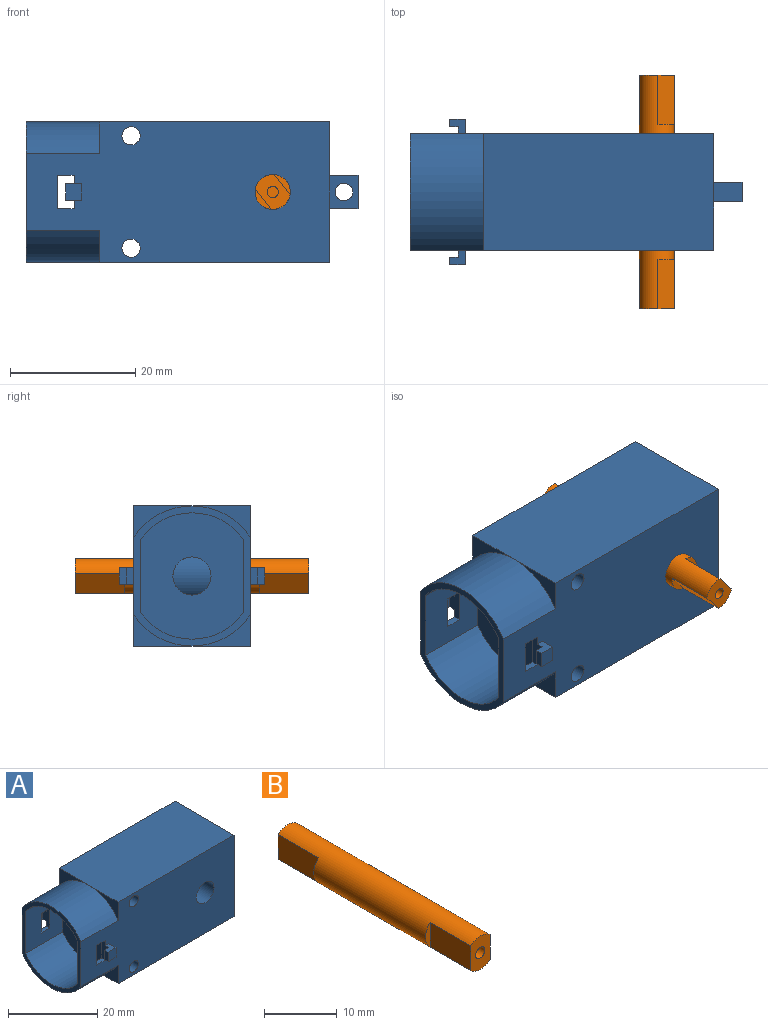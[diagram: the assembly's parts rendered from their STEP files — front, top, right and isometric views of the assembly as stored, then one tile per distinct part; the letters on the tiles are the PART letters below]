
ASSEMBLY  parts=2 mates=1
PART A: 63 faces, bbox 53.1x23.3x22.4 mm
  f0: plane 48.6x22.4mm, normal (0,-1,0), area 914.4mm2, adj f20,f21,f22,f23,f25,f26,f27,f28
  f1: plane 48.6x22.4mm, normal (0,1,0), area 914.4mm2, adj f19,f22,f23,f24,f25,f26,f27,f28
  f2: plane 15.7x0.64mm, normal (0,0,-1), area 10mm2, adj f6,f7,f11,f12
  f3: plane 15.7x0.64mm, normal (0,0,1), area 10mm2, adj f6,f10,f11,f12
  f4: plane 19.4x15.7mm, normal (-1,0,0), area 304.3mm2, adj f5,f9,f11,f12,f13,f14,f16,f17
  f5: plane 27.44x15.7mm, normal (0,0,-1), area 430.8mm2, adj f4,f7,f11,f12
  f6: plane 19.4x15.7mm, normal (1,0,0), area 275.4mm2, adj f2,f3,f11,f12,f18
  f7: cylinder r=2.95mm len=15.7mm, axis (0,1,0), area 168.3mm2, adj f2,f5,f11,f12
  f8: cylinder r=4.3mm len=15.7mm, axis (0,1,0), area 424.2mm2, adj f11,f12
  f9: plane 27.44x15.7mm, normal (0,0,1), area 430.8mm2, adj f4,f10,f11,f12
  f10: cylinder r=2.95mm len=15.7mm, axis (0,1,0), area 168.3mm2, adj f3,f9,f11,f12
  f11: plane 33.8x19.4mm, normal (0,1,0), area 561.9mm2, adj f2,f3,f4,f5,f6,f7,f8,f9
  f12: plane 33.8x19.4mm, normal (0,-1,0), area 561.9mm2, adj f2,f3,f4,f5,f6,f7,f8,f9
  f13: plane 1.11x0.1mm, normal (0,0,1), area 0.1mm2, adj f4,f15,f16,f17
  f14: plane 1.11x0.1mm, normal (0,0,-1), area 0.1mm2, adj f4,f15,f16,f17
  f15: cylinder r=2.9mm len=2.4mm, axis (0,1,0), area 0.2mm2, adj f13,f14,f16,f17
  f16: plane 2.4x1.11mm, normal (0,1,0), area 2.2mm2, adj f4,f13,f14,f15
  f17: plane 2.4x1.11mm, normal (0,-1,0), area 2.2mm2, adj f4,f13,f14,f15
  f18: cylinder r=3.05mm len=6.1mm, axis (-1,0,0), area 28.7mm2, adj f6,f42
  f19: plane 9.35x5.03mm, normal (-1,0,0), area 13.9mm2, adj f1,f27,f36
  f20: plane 9.35x5.03mm, normal (-1,0,0), area 13.9mm2, adj f0,f27,f36
  f21: plane 9.35x5.03mm, normal (-1,0,0), area 13.9mm2, adj f0,f23,f35
  f22: plane 22.4x18.7mm, normal (1,0,0), area 402.1mm2, adj f0,f1,f23,f27,f29,f31,f33,f34
  f23: plane 36.8x18.7mm, normal (0,0,1), area 688.2mm2, adj f0,f1,f21,f22,f24
  f24: plane 9.35x5.03mm, normal (-1,0,0), area 13.9mm2, adj f1,f23,f35
  f25: cylinder r=1.45mm len=18.7mm, axis (0,1,0), area 170.4mm2, adj f0,f1
  f26: cylinder r=2.8mm len=18.7mm, axis (0,1,0), area 329mm2, adj f0,f1
  f27: plane 36.8x18.7mm, normal (0,0,-1), area 688.2mm2, adj f0,f1,f19,f20,f22
  f28: cylinder r=1.45mm len=18.7mm, axis (0,1,0), area 170.4mm2, adj f0,f1
  f29: plane 4.5x3.1mm, normal (0,0,-1), area 13.9mm2, adj f22,f30,f33,f34
  f30: plane 5.4x3.1mm, normal (1,0,0), area 16.7mm2, adj f29,f31,f33,f34
  f31: plane 4.5x3.1mm, normal (0,0,1), area 13.9mm2, adj f22,f30,f33,f34
  f32: cylinder r=1.4mm len=3.1mm, axis (0,1,0), area 27.3mm2, adj f33,f34
  f33: plane 5.4x4.5mm, normal (0,-1,0), area 18.1mm2, adj f22,f29,f30,f31,f32
  f34: plane 5.4x4.5mm, normal (0,1,0), area 18.1mm2, adj f22,f29,f30,f31,f32
  f35: cylinder r=11.2mm len=18.7mm, axis (1,0,0), area 261.1mm2, adj f0,f1,f21,f24,f37
  f36: cylinder r=11.2mm len=18.7mm, axis (1,0,0), area 261.1mm2, adj f0,f1,f19,f20,f37
  f37: plane 22.4x18.7mm, normal (-1,0,0), area 72mm2, adj f0,f1,f35,f36,f38,f39,f40,f41
  f38: cylinder r=10.1mm len=16.5mm, axis (-1,0,0), area 227.8mm2, adj f37,f39,f41,f42
  f39: plane 11.8x11.65mm, normal (0,-1,0), area 122.9mm2, adj f37,f38,f40,f42,f47,f48,f49,f50
  f40: cylinder r=10.1mm len=16.5mm, axis (-1,0,0), area 227.8mm2, adj f37,f39,f41,f42
  f41: plane 11.8x11.65mm, normal (0,1,0), area 122.9mm2, adj f37,f38,f40,f42,f43,f44,f45,f46
  f42: plane 20.2x16.5mm, normal (-1,0,0), area 261.9mm2, adj f18,f38,f39,f40,f41
  f43: plane 2.7x1.1mm, normal (0,0,-1), area 3mm2, adj f0,f41,f44,f46
  f44: plane 5.4x2.2mm, normal (-1,0,0), area 8.8mm2, adj f0,f41,f43,f45,f60,f61,f62
  f45: plane 2.7x1.1mm, normal (0,0,1), area 3mm2, adj f0,f41,f44,f46
  f46: plane 5.4x1.1mm, normal (1,0,0), area 5.9mm2, adj f0,f41,f43,f45
  f47: plane 5.4x1.1mm, normal (1,0,0), area 5.9mm2, adj f1,f39,f48,f50
  f48: plane 2.7x1.1mm, normal (0,0,1), area 3mm2, adj f1,f39,f47,f49
  f49: plane 5.4x2.2mm, normal (-1,0,0), area 8.8mm2, adj f1,f39,f48,f50,f54,f55,f56
  f50: plane 2.7x1.1mm, normal (0,0,-1), area 3mm2, adj f1,f39,f47,f49
  f51: plane 2.6x2.3mm, normal (1,0,0), area 6mm2, adj f1,f52,f55,f56
  f52: plane 2.6x2.5mm, normal (0,1,0), area 6.5mm2, adj f51,f53,f55,f56
  f53: plane 2.6x1.2mm, normal (-1,0,0), area 3.1mm2, adj f52,f54,f55,f56
  f54: plane 2.6x1.35mm, normal (0,-1,0), area 3.5mm2, adj f49,f53,f55,f56
  f55: plane 2.5x2.3mm, normal (0,0,1), area 4.3mm2, adj f1,f49,f51,f52,f53,f54
  f56: plane 2.5x2.3mm, normal (0,0,-1), area 4.3mm2, adj f1,f49,f51,f52,f53,f54
  f57: plane 2.6x2.3mm, normal (1,0,0), area 6mm2, adj f0,f58,f61,f62
  f58: plane 2.6x2.5mm, normal (0,-1,0), area 6.5mm2, adj f57,f59,f61,f62
  f59: plane 2.6x1.2mm, normal (-1,0,0), area 3.1mm2, adj f58,f60,f61,f62
  f60: plane 2.6x1.35mm, normal (0,1,0), area 3.5mm2, adj f44,f59,f61,f62
  f61: plane 2.5x2.3mm, normal (0,0,1), area 4.3mm2, adj f0,f44,f57,f58,f59,f60
  f62: plane 2.5x2.3mm, normal (0,0,-1), area 4.3mm2, adj f0,f44,f57,f58,f59,f60
PART B: 15 faces, bbox 5.6x37.4x5.6 mm
  f0: cylinder r=2.8mm len=37.4mm, axis (0,-1,0), area 511.2mm2, adj f1,f2,f3,f4,f5,f8,f9,f10
  f1: plane 5.6x3.76mm, normal (0,1,0), area 16.8mm2, adj f0,f2,f4,f6
  f2: plane 7.85x4.15mm, normal (1,0,0), area 32.6mm2, adj f0,f1,f3
  f3: plane 4.15x0.92mm, normal (0,1,0), area 2.6mm2, adj f0,f2
  f4: plane 7.85x4.15mm, normal (-1,0,0), area 32.6mm2, adj f0,f1,f5
  f5: plane 4.15x0.92mm, normal (0,1,0), area 2.6mm2, adj f0,f4
  f6: cylinder r=0.9mm len=7.85mm, axis (0,1,0), area 44.4mm2, adj f1,f7
  f7: plane 1.8x1.8mm, normal (0,1,0), area 2.5mm2, adj f6
  f8: plane 5.6x3.76mm, normal (0,-1,0), area 16.8mm2, adj f0,f9,f11,f13
  f9: plane 7.85x4.15mm, normal (1,0,0), area 32.6mm2, adj f0,f8,f10
  f10: plane 4.15x0.92mm, normal (0,-1,0), area 2.6mm2, adj f0,f9
  f11: plane 7.85x4.15mm, normal (-1,0,0), area 32.6mm2, adj f0,f8,f12
  f12: plane 4.15x0.92mm, normal (0,-1,0), area 2.6mm2, adj f0,f11
  f13: cylinder r=0.9mm len=7.85mm, axis (0,-1,0), area 44.4mm2, adj f8,f14
  f14: plane 1.8x1.8mm, normal (0,-1,0), area 2.5mm2, adj f13
PLACE A t=(-46.81,-21.73,-0.08)mm fixed
PLACE B rot(axis=(0,-1,0),38.1deg) t=(-44.83,-21.73,-5.8)mm
MATE revolute A.f8 <-> B.f0  axis (0,1,0) through (-37.55,-21.73,-0.08)mm
